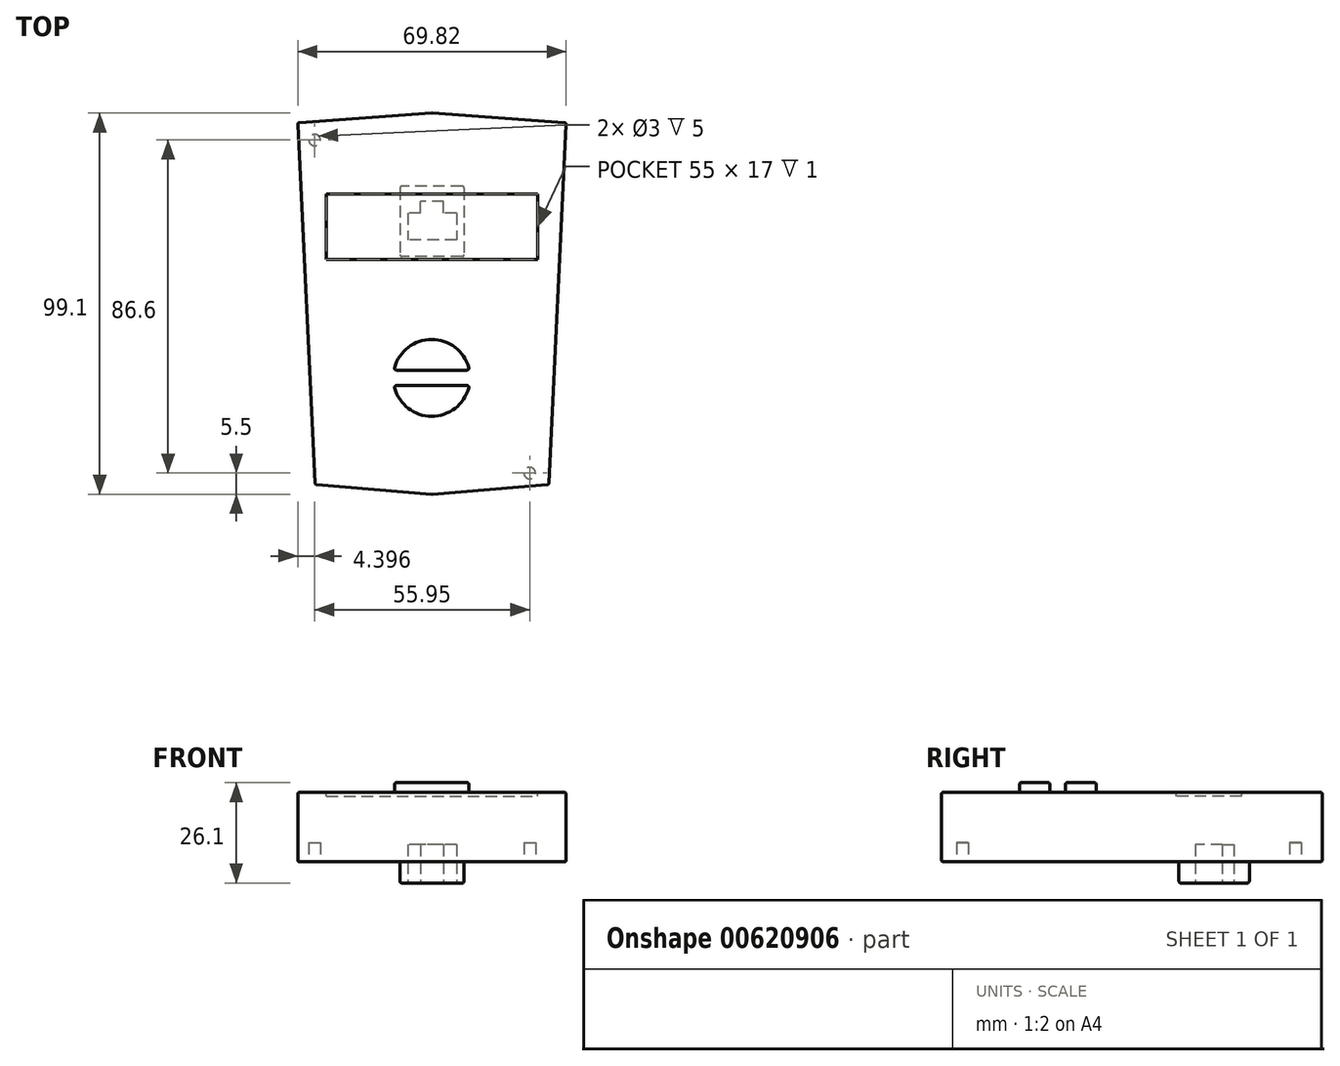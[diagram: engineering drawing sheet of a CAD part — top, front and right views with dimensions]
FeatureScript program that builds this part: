
annotation { "Feature Type Name" : "Feature", "Feature Type Description" : "" }
export const myFeature = defineFeature(function(context is Context, id is Id, definition is map)
    precondition{}
    {
        {
            var Q0;
            Q0=qCreatedBy(makeId("Top.planeOp"),FACE);
            var sketch = newSketch(context, id + "F0", { "sketchPlane" : qUnion([Q0])});
            skLineSegment(sketch, "E0.bottom", {"start": v(0, 0) * mm, "end": v(70.1, 0) * mm});
            skLineSegment(sketch, "E0.top", {"start": v(0, -99.1) * mm, "end": v(70.1, -99.1) * mm});
            skLineSegment(sketch, "E0.left", {"start": v(0, 0) * mm, "end": v(0, -99.1) * mm});
            skLineSegment(sketch, "E0.right", {"start": v(70.1, 0) * mm, "end": v(70.1, -99.1) * mm});
            skLineSegment(sketch, "E1", {"start": v(70.1, 0) * mm, "end": v(65.35, -99.1) * mm});
            skLineSegment(sketch, "E2", {"start": v(0, 0) * mm, "end": v(4.75, -99.1) * mm});
            skLineSegment(sketch, "E3", {"start": v(35.05, -99.1) * mm, "end": v(4.63, -96.6) * mm});
            skLineSegment(sketch, "E4", {"start": v(35.05, -99.1) * mm, "end": v(65.47, -96.6) * mm});
            skLineSegment(sketch, "E5", {"start": v(35.05, 0) * mm, "end": v(69.98, -2.5) * mm});
            skLineSegment(sketch, "E6", {"start": v(35.05, 0) * mm, "end": v(0.12, -2.5) * mm});
            skSolve(sketch);
        }
        {
            var Q0;
            {var subQ1=sQuery(id+"F0.wireOp",EDGE,"E3");Q0=makeQuery(id+"F0.imprint","IMPRINT",FACE,{"disambiguationData":[TD([[makeQuery(id+"F0.imprint","IMPRINT",EDGE,{"derivedFrom":subQ1}),-1.0]])]});}
            extrude(context, id + "F1", {"entities" : qUnion([Q0]), "depth" : 18.1 * mm, "offsetDistance" : 25 * mm});
        }
        {
            var Q0;
            Q0=makeQuery(id+"F1.opExtrude","CAP_FACE",FACE,{"disambiguationData":[OSD([sQuery(id+"F0.wireOp",EDGE,"E1"),sQuery(id+"F0.wireOp",EDGE,"E2"),sQuery(id+"F0.wireOp",EDGE,"E3"),sQuery(id+"F0.wireOp",EDGE,"E4"),sQuery(id+"F0.wireOp",EDGE,"E5"),sQuery(id+"F0.wireOp",EDGE,"E6")])],"isStart":false});
            var sketch = newSketch(context, id + "F2", { "sketchPlane" : qUnion([Q0])});
            skCircle(sketch, "E7", {"center": v(34.98, -68.82) * mm, "radius": 10 * mm});
            skLineSegment(sketch, "E8", {"start": v(25.18, -70.82) * mm, "end": v(44.78, -70.82) * mm});
            skLineSegment(sketch, "E9", {"start": v(25.18, -66.82) * mm, "end": v(44.78, -66.82) * mm});
            skSolve(sketch);
        }
        {
            var Q0;
            {var subQ0=sQuery(id+"F2.wireOp",EDGE,"E9");Q0=makeQuery(id+"F2.imprint","IMPRINT",FACE,{"disambiguationData":[TD([[makeQuery(id+"F2.imprint","IMPRINT",EDGE,{"derivedFrom":subQ0}),1.0]])]});}
            var Q1;
            {var subQ0=sQuery(id+"F2.wireOp",EDGE,"E8");Q1=makeQuery(id+"F2.imprint","IMPRINT",FACE,{"disambiguationData":[TD([[makeQuery(id+"F2.imprint","IMPRINT",EDGE,{"derivedFrom":subQ0}),-1.0]])]});}
            extrude(context, id + "F3", {"entities" : qUnion([Q0, Q1]), "operationType" : NewBodyOperationType.ADD, "depth" : 2.5 * mm, "offsetDistance" : 25 * mm});
        }
        {
            var Q0;
            Q0=makeQuery(id+"F1.opExtrude","CAP_FACE",FACE,{"disambiguationData":[OSD([sQuery(id+"F0.wireOp",EDGE,"E1"),sQuery(id+"F0.wireOp",EDGE,"E2"),sQuery(id+"F0.wireOp",EDGE,"E3"),sQuery(id+"F0.wireOp",EDGE,"E4"),sQuery(id+"F0.wireOp",EDGE,"E5"),sQuery(id+"F0.wireOp",EDGE,"E6")])],"isStart":false});
            var sketch = newSketch(context, id + "F4", { "sketchPlane" : qUnion([Q0])});
            skLineSegment(sketch, "E10.bottom", {"start": v(7.55, -21) * mm, "end": v(62.55, -21) * mm});
            skLineSegment(sketch, "E10.top", {"start": v(7.55, -38) * mm, "end": v(62.55, -38) * mm});
            skLineSegment(sketch, "E10.left", {"start": v(7.55, -21) * mm, "end": v(7.55, -38) * mm});
            skLineSegment(sketch, "E10.right", {"start": v(62.55, -21) * mm, "end": v(62.55, -38) * mm});
            skSolve(sketch);
        }
        {
            var Q0;
            Q0 = qSketchRegion(id + "F4", true);
            extrude(context, id + "F5", {"entities" : qUnion([Q0]), "operationType" : NewBodyOperationType.REMOVE, "oppositeDirection" : true, "depth" : 1 * mm, "offsetDistance" : 25 * mm});
        }
        {
            var Q0;
            Q0=makeQuery(id+"F3.opExtrude","CAP_FACE",FACE,{"disambiguationData":[OSD([sQuery(id+"F2.wireOp",EDGE,"E7"),sQuery(id+"F2.wireOp",EDGE,"E9")])],"isStart":false});
            var Q1;
            Q1=makeQuery(id+"F3.opExtrude","CAP_FACE",FACE,{"disambiguationData":[OSD([sQuery(id+"F2.wireOp",EDGE,"E7"),sQuery(id+"F2.wireOp",EDGE,"E8")])],"isStart":false});
            var Q2;
            {var subQ0=sQuery(id+"F2.wireOp",EDGE,"E8");var subQ1=sQuery(id+"F2.wireOp",EDGE,"E7");Q2=makeQuery(id+"F3.opExtrude","SWEPT_EDGE",EDGE,{"disambiguationData":[OSD([subQ1,subQ0]),TDD([makeQuery(id+"F2.imprint","INTERSECT",VERTEX,{"disambiguationData":[OD(0.0)],"derivedFrom":[subQ1,subQ0]})])]});}
            var Q3;
            {var subQ0=sQuery(id+"F2.wireOp",EDGE,"E9");var subQ1=sQuery(id+"F2.wireOp",EDGE,"E7");Q3=makeQuery(id+"F3.opExtrude","SWEPT_EDGE",EDGE,{"disambiguationData":[OSD([subQ1,subQ0]),TDD([makeQuery(id+"F2.imprint","INTERSECT",VERTEX,{"disambiguationData":[OD(0.0)],"derivedFrom":[subQ1,subQ0]})])]});}
            var Q4;
            {var subQ0=sQuery(id+"F2.wireOp",EDGE,"E9");var subQ1=sQuery(id+"F2.wireOp",EDGE,"E7");Q4=makeQuery(id+"F3.opExtrude","SWEPT_EDGE",EDGE,{"disambiguationData":[OSD([subQ1,subQ0]),TDD([makeQuery(id+"F2.imprint","INTERSECT",VERTEX,{"disambiguationData":[OD(1.0)],"derivedFrom":[subQ1,subQ0]})])]});}
            var Q5;
            {var subQ0=sQuery(id+"F2.wireOp",EDGE,"E8");var subQ1=sQuery(id+"F2.wireOp",EDGE,"E7");Q5=makeQuery(id+"F3.opExtrude","SWEPT_EDGE",EDGE,{"disambiguationData":[OSD([subQ1,subQ0]),TDD([makeQuery(id+"F2.imprint","INTERSECT",VERTEX,{"disambiguationData":[OD(1.0)],"derivedFrom":[subQ1,subQ0]})])]});}
            var Q6;
            Q6=makeQuery(id+"F1.opExtrude","SWEPT_FACE",FACE,{"disambiguationData":[OSD([sQuery(id+"F0.wireOp",EDGE,"E1")])]});
            var Q7;
            Q7=makeQuery(id+"F1.opExtrude","SWEPT_FACE",FACE,{"disambiguationData":[OSD([sQuery(id+"F0.wireOp",EDGE,"E4")])]});
            var Q8;
            Q8=makeQuery(id+"F1.opExtrude","SWEPT_FACE",FACE,{"disambiguationData":[OSD([sQuery(id+"F0.wireOp",EDGE,"E3")])]});
            var Q9;
            Q9=makeQuery(id+"F1.opExtrude","SWEPT_FACE",FACE,{"disambiguationData":[OSD([sQuery(id+"F0.wireOp",EDGE,"E2")])]});
            var Q10;
            Q10=makeQuery(id+"F1.opExtrude","SWEPT_FACE",FACE,{"disambiguationData":[OSD([sQuery(id+"F0.wireOp",EDGE,"E6")])]});
            var Q11;
            Q11=makeQuery(id+"F1.opExtrude","SWEPT_FACE",FACE,{"disambiguationData":[OSD([sQuery(id+"F0.wireOp",EDGE,"E5")])]});
            var Q12;
            Q12=makeQuery(id+"F1.opExtrude","SWEPT_EDGE",EDGE,{"disambiguationData":[OSD([sQuery(id+"F0.wireOp",EDGE,"E0.bottom"),sQuery(id+"F0.wireOp",EDGE,"E5"),sQuery(id+"F0.wireOp",EDGE,"E6")])]});
            var Q13;
            Q13=makeQuery(id+"F1.opExtrude","SWEPT_EDGE",EDGE,{"disambiguationData":[OSD([sQuery(id+"F0.wireOp",EDGE,"E0.top"),sQuery(id+"F0.wireOp",EDGE,"E3"),sQuery(id+"F0.wireOp",EDGE,"E4")])]});
            fillet(context, id + "F6", {"entities" : qUnion([Q0, Q1, Q2, Q3, Q4, Q5, Q6, Q7, Q8, Q9, Q10, Q11, Q12, Q13]), "radius" : 0.5 * mm, "tangentPropagation" : true, "allowEdgeOverflow" : false});
        }
        {
            var Q0;
            Q0=makeQuery(id+"F1.opExtrude","CAP_FACE",FACE,{"disambiguationData":[OSD([sQuery(id+"F0.wireOp",EDGE,"E1"),sQuery(id+"F0.wireOp",EDGE,"E2"),sQuery(id+"F0.wireOp",EDGE,"E3"),sQuery(id+"F0.wireOp",EDGE,"E4"),sQuery(id+"F0.wireOp",EDGE,"E5"),sQuery(id+"F0.wireOp",EDGE,"E6")])],"isStart":true});
            var sketch = newSketch(context, id + "F7", { "sketchPlane" : qUnion([Q0])});
            skLineSegment(sketch, "E11.bottom", {"start": v(43.44, 19) * mm, "end": v(26.74, 19) * mm});
            skLineSegment(sketch, "E11.top", {"start": v(43.44, 37.3) * mm, "end": v(26.74, 37.3) * mm});
            skLineSegment(sketch, "E11.left", {"start": v(43.44, 19) * mm, "end": v(43.44, 37.3) * mm});
            skLineSegment(sketch, "E11.right", {"start": v(26.74, 19) * mm, "end": v(26.74, 37.3) * mm});
            skSolve(sketch);
        }
        {
            var Q0;
            Q0 = qSketchRegion(id + "F7", true);
            extrude(context, id + "F8", {"entities" : qUnion([Q0]), "operationType" : NewBodyOperationType.ADD, "depth" : 5.5 * mm, "offsetDistance" : 25 * mm});
        }
        {
            var Q0;
            Q0=makeQuery(id+"F8.opExtrude","CAP_FACE",FACE,{"disambiguationData":[OSD([sQuery(id+"F7.wireOp",EDGE,"E11.bottom"),sQuery(id+"F7.wireOp",EDGE,"E11.top"),sQuery(id+"F7.wireOp",EDGE,"E11.left"),sQuery(id+"F7.wireOp",EDGE,"E11.right")])],"isStart":false});
            var Q1;
            Q1=makeQuery(id+"F8.opExtrude","SWEPT_EDGE",EDGE,{"disambiguationData":[OSD([sQuery(id+"F7.wireOp",EDGE,"E11.bottom"),sQuery(id+"F7.wireOp",EDGE,"E11.left")])]});
            var Q2;
            Q2=makeQuery(id+"F8.opExtrude","SWEPT_EDGE",EDGE,{"disambiguationData":[OSD([sQuery(id+"F7.wireOp",EDGE,"E11.bottom"),sQuery(id+"F7.wireOp",EDGE,"E11.right")])]});
            var Q3;
            Q3=makeQuery(id+"F8.opExtrude","SWEPT_EDGE",EDGE,{"disambiguationData":[OSD([sQuery(id+"F7.wireOp",EDGE,"E11.top"),sQuery(id+"F7.wireOp",EDGE,"E11.right")])]});
            var Q4;
            Q4=makeQuery(id+"F8.opExtrude","SWEPT_EDGE",EDGE,{"disambiguationData":[OSD([sQuery(id+"F7.wireOp",EDGE,"E11.top"),sQuery(id+"F7.wireOp",EDGE,"E11.left")])]});
            fillet(context, id + "F9", {"entities" : qUnion([Q0, Q1, Q2, Q3, Q4]), "radius" : .5 * mm, "tangentPropagation" : true, "allowEdgeOverflow" : false});
        }
        {
            var Q0;
            Q0=makeQuery(id+"F8.opExtrude","CAP_FACE",FACE,{"disambiguationData":[OSD([sQuery(id+"F7.wireOp",EDGE,"E11.bottom"),sQuery(id+"F7.wireOp",EDGE,"E11.top"),sQuery(id+"F7.wireOp",EDGE,"E11.left"),sQuery(id+"F7.wireOp",EDGE,"E11.right")])],"isStart":false});
            var sketch = newSketch(context, id + "F10", { "sketchPlane" : qUnion([Q0])});
            skLineSegment(sketch, "E12.bottom", {"start": v(41.44, 26) * mm, "end": v(28.74, 26) * mm});
            skLineSegment(sketch, "E12.top", {"start": v(41.44, 33) * mm, "end": v(28.74, 33) * mm});
            skLineSegment(sketch, "E12.left", {"start": v(41.44, 26) * mm, "end": v(41.44, 33) * mm});
            skLineSegment(sketch, "E12.right", {"start": v(28.74, 26) * mm, "end": v(28.74, 33) * mm});
            skLineSegment(sketch, "E13.bottom", {"start": v(38.09, 26) * mm, "end": v(32.09, 26) * mm});
            skLineSegment(sketch, "E13.top", {"start": v(38.09, 23) * mm, "end": v(32.09, 23) * mm});
            skLineSegment(sketch, "E13.left", {"start": v(38.09, 26) * mm, "end": v(38.09, 23) * mm});
            skLineSegment(sketch, "E13.right", {"start": v(32.09, 26) * mm, "end": v(32.09, 23) * mm});
            skSolve(sketch);
        }
        {
            var Q0;
            Q0 = qSketchRegion(id + "F10", true);
            extrude(context, id + "F11", {"entities" : qUnion([Q0]), "operationType" : NewBodyOperationType.REMOVE, "oppositeDirection" : true, "depth" : 10 * mm, "offsetDistance" : 25 * mm});
        }
        {
            var Q0;
            Q0=makeQuery(id+"F1.opExtrude","CAP_FACE",FACE,{"disambiguationData":[OSD([sQuery(id+"F0.wireOp",EDGE,"E1"),sQuery(id+"F0.wireOp",EDGE,"E2"),sQuery(id+"F0.wireOp",EDGE,"E3"),sQuery(id+"F0.wireOp",EDGE,"E4"),sQuery(id+"F0.wireOp",EDGE,"E5"),sQuery(id+"F0.wireOp",EDGE,"E6")])],"isStart":true});
            var sketch = newSketch(context, id + "F12", { "sketchPlane" : qUnion([Q0])});
            skCircle(sketch, "E14", {"center": v(4.54, 7) * mm, "radius": 1.5 * mm});
            skCircle(sketch, "E15", {"center": v(60.49, 93.6) * mm, "radius": 1.5 * mm});
            skSolve(sketch);
        }
        {
            var Q0;
            Q0 = qSketchRegion(id + "F12", true);
            extrude(context, id + "F13", {"entities" : qUnion([Q0]), "operationType" : NewBodyOperationType.REMOVE, "oppositeDirection" : true, "depth" : 5 * mm, "offsetDistance" : 25 * mm});
        }
    });
